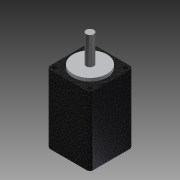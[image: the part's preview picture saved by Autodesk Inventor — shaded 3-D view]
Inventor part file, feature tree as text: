
AUTODESK INVENTOR PART (.ipt)
format: ipt  version: 2014 SP2 (Build 180246200, 246)  size: 139,776 bytes
history: native  units: mm
features: sketch x4, extrude x3, fillet x2, hole x1
ambient origin geometry x8: Origin, YZ Plane, XZ Plane, XY Plane, X Axis, Y Axis, Z Axis, Center Point
bodies: Solid1 (feature_tree)
feature tree (10):
  extrude  "Extrusion1"  Depth=28.2mm
  extrude  "Extrusion2"  Depth=45.0mm
  extrude  "Extrusion3"  Depth=2.0mm
  hole  "Hole1"  [1 undecoded]
  fillet  "Fillet1"  Radius=11.5mm
  fillet  "Fillet2"  Radius=11.5mm
  sketch  "Sketch1"  dims[d0=28.2mm d1=28.2mm]
  sketch  "Sketch2"  dims[d2=45.0mm d3=0.0mm d4=22.0mm]
  sketch  "Sketch3"  dims[d5=2.0mm d6=0.0mm d7=5.0mm]
  sketch  "Sketch4"  dims[d8=18.0mm d9=0.0mm d10=11.5mm d11=11.5mm d12=11.5mm d13=11.5mm d14=11.5mm d15=11.5mm d16=11.5mm d17=11.5mm d18=2.5mm d19=6.0mm d20=4.0mm d21=2.0mm d22=90.0deg d23=4.5mm d24=20.594885mm d25=2.5mm d26=1.0mm]
note: 1 required parameter value undecoded (feature->parameter linkage not recoverable at this tier; creation-order binding heuristic only, values carry confidence <= 0.55)
